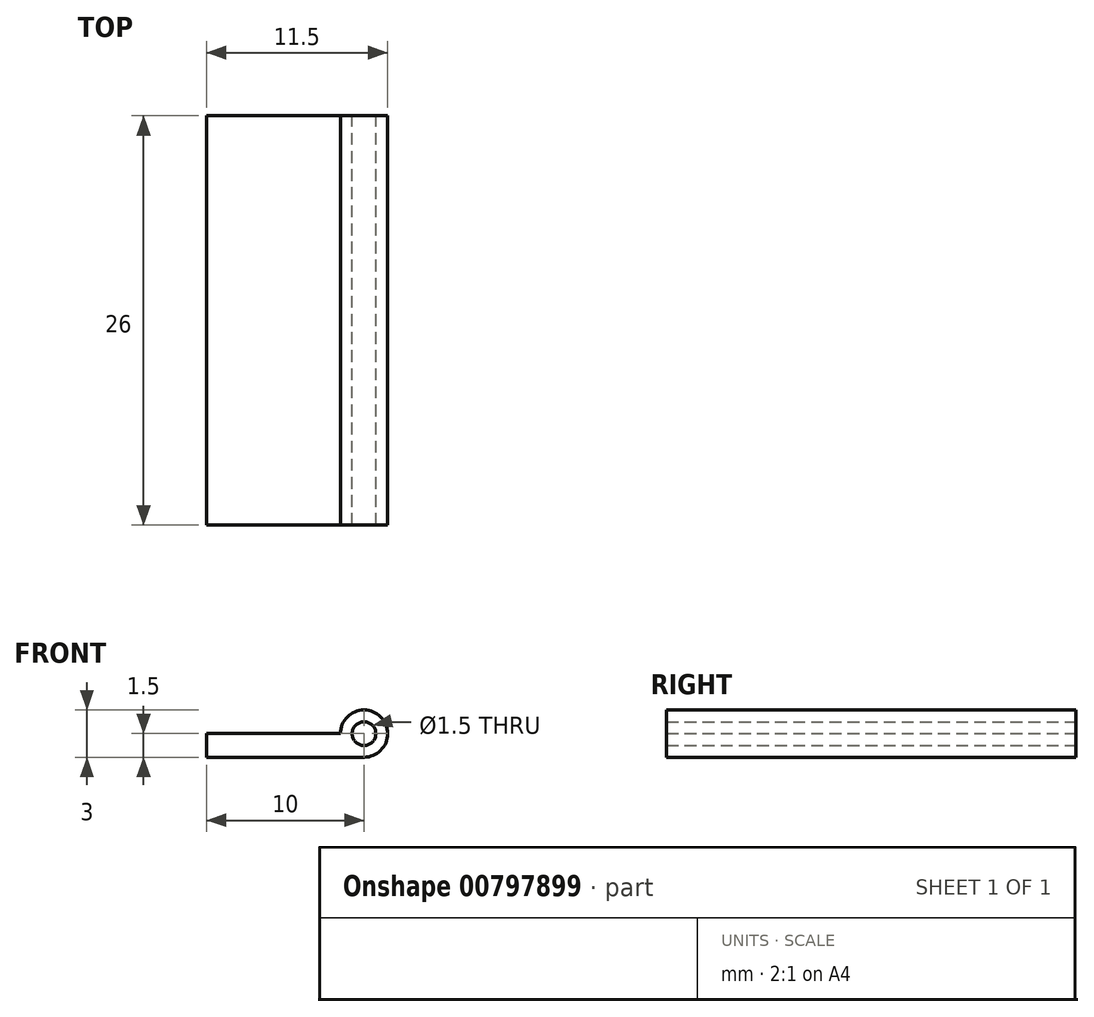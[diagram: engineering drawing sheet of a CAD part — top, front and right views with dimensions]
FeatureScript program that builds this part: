
annotation { "Feature Type Name" : "Feature", "Feature Type Description" : "" }
export const myFeature = defineFeature(function(context is Context, id is Id, definition is map)
    precondition{}
    {
        {
            var Q0;
            Q0=qCreatedBy(makeId("Front.planeOp"),FACE);
            var sketch = newSketch(context, id + "F0", { "sketchPlane" : qUnion([Q0])});
            skCircle(sketch, "E0", {"center": v(0, 0) * mm, "radius": 1.5 * mm});
            skSolve(sketch);
        }
        {
            var Q0;
            Q0 = qSketchRegion(id + "F0", true);
            extrude(context, id + "F1", {"entities" : qUnion([Q0]), "depth" : 26 * mm, "offsetDistance" : 25 * mm});
        }
        {
            var Q0;
            Q0=qCreatedBy(makeId("Front.planeOp"),FACE);
            var sketch = newSketch(context, id + "F2", { "sketchPlane" : qUnion([Q0])});
            skLineSegment(sketch, "E1.bottom", {"start": v(0, 0) * mm, "end": v(-10, 0) * mm});
            skLineSegment(sketch, "E1.top", {"start": v(0, -1.5) * mm, "end": v(-10, -1.5) * mm});
            skLineSegment(sketch, "E1.left", {"start": v(0, 0) * mm, "end": v(0, -1.5) * mm});
            skLineSegment(sketch, "E1.right", {"start": v(-10, 0) * mm, "end": v(-10, -1.5) * mm});
            skSolve(sketch);
        }
        {
            var Q0;
            Q0 = qSketchRegion(id + "F2", true);
            extrude(context, id + "F3", {"entities" : qUnion([Q0]), "operationType" : NewBodyOperationType.ADD, "depth" : 26 * mm, "offsetDistance" : 25 * mm});
        }
        {
            var Q0;
            Q0=qCreatedBy(makeId("Front.planeOp"),FACE);
            var sketch = newSketch(context, id + "F4", { "sketchPlane" : qUnion([Q0])});
            skCircle(sketch, "E2", {"center": v(0, 0) * mm, "radius": 0.75 * mm});
            skSolve(sketch);
        }
        {
            var Q0;
            Q0 = qSketchRegion(id + "F4", true);
            extrude(context, id + "F5", {"entities" : qUnion([Q0]), "operationType" : NewBodyOperationType.REMOVE, "depth" : 28.9 * mm, "offsetDistance" : 25 * mm});
        }
    });
